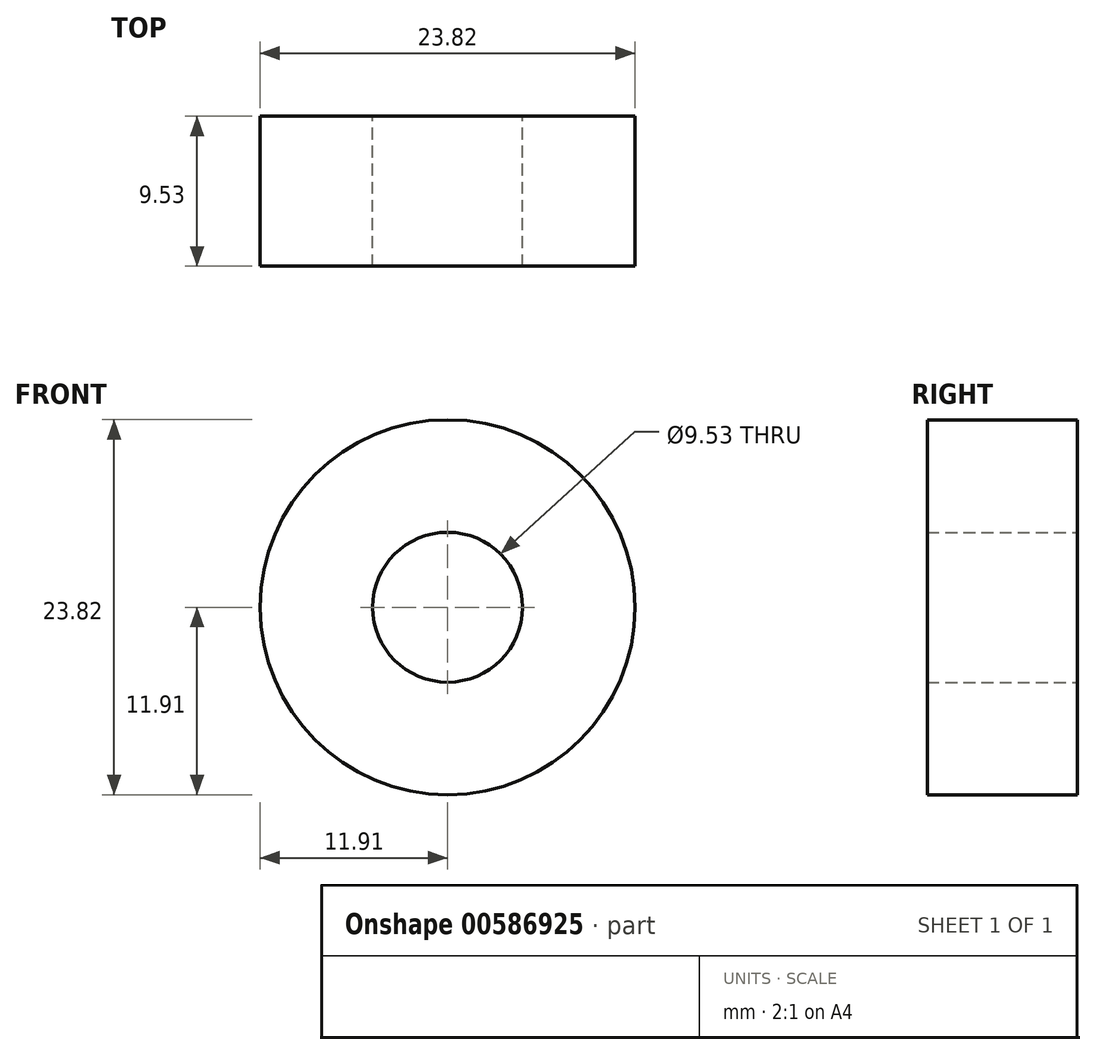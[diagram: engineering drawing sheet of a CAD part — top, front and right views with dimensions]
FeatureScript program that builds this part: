
annotation { "Feature Type Name" : "Feature", "Feature Type Description" : "" }
export const myFeature = defineFeature(function(context is Context, id is Id, definition is map)
    precondition{}
    {
        {
            var Q0;
            Q0=qCreatedBy(makeId("Front.planeOp"),FACE);
            var sketch = newSketch(context, id + "F0", { "sketchPlane" : qUnion([Q0])});
            skCircle(sketch, "E0", {"center": v(0, 0) * mm, "radius": 11.9 * mm});
            skCircle(sketch, "E1", {"center": v(0, 0) * mm, "radius": 4.76 * mm});
            skSolve(sketch);
        }
        {
            var Q0;
            Q0 = qSketchRegion(id + "F0", true);
            extrude(context, id + "F1", {"entities" : qUnion([Q0]), "depth" : 9.52 * mm, "offsetDistance" : 25.4 * mm});
        }
    });
